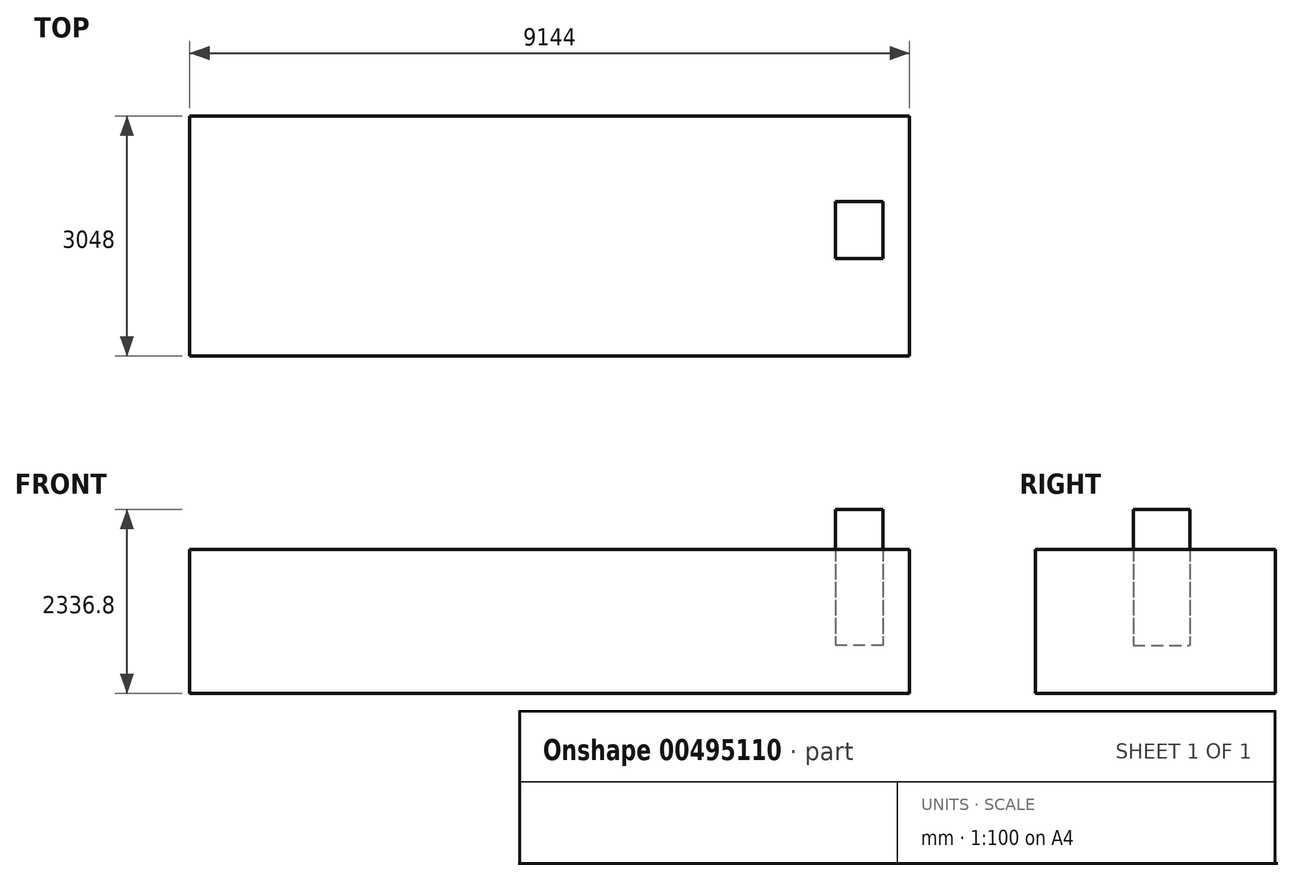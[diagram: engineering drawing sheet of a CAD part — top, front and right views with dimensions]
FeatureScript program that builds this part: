
annotation { "Feature Type Name" : "Feature", "Feature Type Description" : "" }
export const myFeature = defineFeature(function(context is Context, id is Id, definition is map)
    precondition{}
    {
        {
            var Q0;
            Q0=qCreatedBy(makeId("Top.planeOp"),FACE);
            var sketch = newSketch(context, id + "F0", { "sketchPlane" : qUnion([Q0])});
            skLineSegment(sketch, "E0.bottom", {"start": v(-4572, 1524) * mm, "end": v(4572, 1524) * mm});
            skLineSegment(sketch, "E0.top", {"start": v(-4572, -1524) * mm, "end": v(4572, -1524) * mm});
            skLineSegment(sketch, "E0.left", {"start": v(-4572, 1524) * mm, "end": v(-4572, -1524) * mm});
            skLineSegment(sketch, "E0.right", {"start": v(4572, 1524) * mm, "end": v(4572, -1524) * mm});
            skPoint(sketch, "E0.middle", {"position": v(0, 0) * mm});
            skSolve(sketch);
        }
        {
            var Q0;
            Q0 = qSketchRegion(id + "F0", true);
            extrude(context, id + "F1", {"entities" : qUnion([Q0]), "oppositeDirection" : true, "depth" : 1828.8 * mm});
        }
        {
            var Q0;
            Q0=makeQuery(id+"F1.opExtrude","CAP_FACE",FACE,{"disambiguationData":[OSD([sQuery(id+"F0.wireOp",EDGE,"E0.bottom"),sQuery(id+"F0.wireOp",EDGE,"E0.top"),sQuery(id+"F0.wireOp",EDGE,"E0.left"),sQuery(id+"F0.wireOp",EDGE,"E0.right")])],"isStart":true});
            var sketch = newSketch(context, id + "F2", { "sketchPlane" : qUnion([Q0])});
            skLineSegment(sketch, "E1.bottom", {"start": v(4234.89, -283.35) * mm, "end": v(3628.36, -283.35) * mm});
            skLineSegment(sketch, "E1.top", {"start": v(4234.89, 437.43) * mm, "end": v(3628.36, 437.43) * mm});
            skLineSegment(sketch, "E1.left", {"start": v(4234.89, -283.35) * mm, "end": v(4234.89, 437.43) * mm});
            skLineSegment(sketch, "E1.right", {"start": v(3628.36, -283.35) * mm, "end": v(3628.36, 437.43) * mm});
            skSolve(sketch);
        }
        {
            var Q0;
            Q0 = qSketchRegion(id + "F2", true);
            extrude(context, id + "F3", {"entities" : qUnion([Q0]), "depth" : 508 * mm, "hasSecondDirection" : true, "secondDirectionOppositeDirection" : true, "secondDirectionDepth" : 1219.2 * mm});
        }
    });
